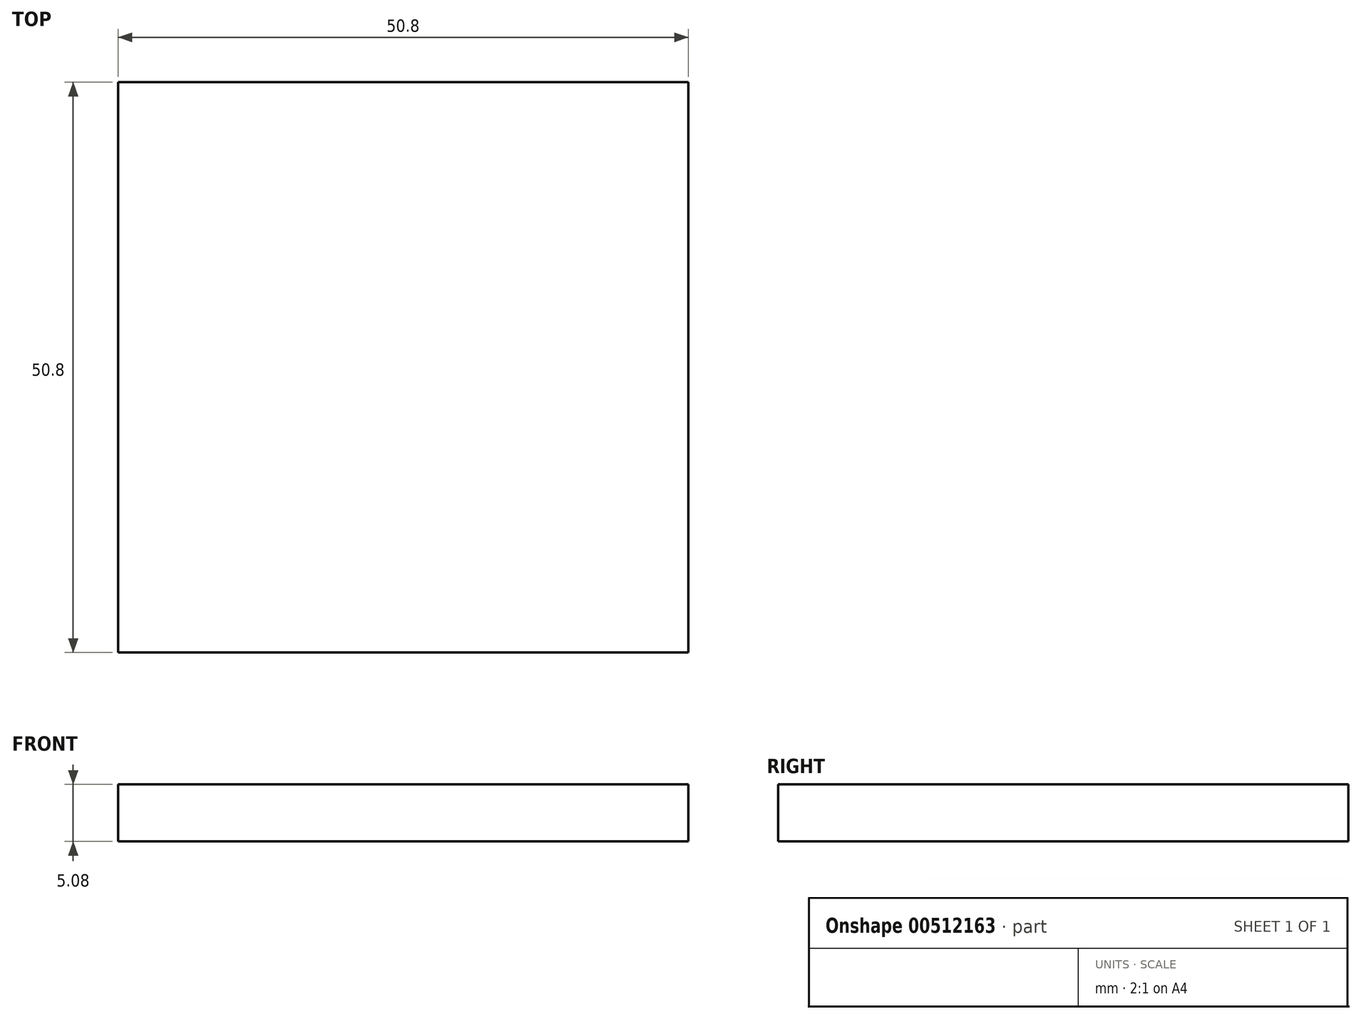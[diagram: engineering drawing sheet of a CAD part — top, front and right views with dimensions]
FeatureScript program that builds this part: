
annotation { "Feature Type Name" : "Feature", "Feature Type Description" : "" }
export const myFeature = defineFeature(function(context is Context, id is Id, definition is map)
    precondition{}
    {
        {
            var Q0;
            Q0=qCreatedBy(makeId("Top.planeOp"),FACE);
            var sketch = newSketch(context, id + "F0", { "sketchPlane" : qUnion([Q0])});
            skLineSegment(sketch, "E0.bottom", {"start": v(-26.12, 16.33) * mm, "end": v(24.68, 16.33) * mm});
            skLineSegment(sketch, "E0.top", {"start": v(-26.12, -34.47) * mm, "end": v(24.68, -34.47) * mm});
            skLineSegment(sketch, "E0.left", {"start": v(-26.12, 16.33) * mm, "end": v(-26.12, -34.47) * mm});
            skLineSegment(sketch, "E0.right", {"start": v(24.68, 16.33) * mm, "end": v(24.68, -34.47) * mm});
            skSolve(sketch);
        }
        {
            var Q0;
            Q0=makeQuery(id+"F0.imprint","IMPRINT",FACE,{"disambiguationData":[TD([[makeQuery(id+"F0.imprint","IMPRINT",EDGE,{"derivedFrom":sQuery(id+"F0.wireOp",EDGE,"E0.bottom")}),-1.0]])]});
            extrude(context, id + "F1", {"entities" : qUnion([Q0]), "depth" : 5.08 * mm});
        }
    });
